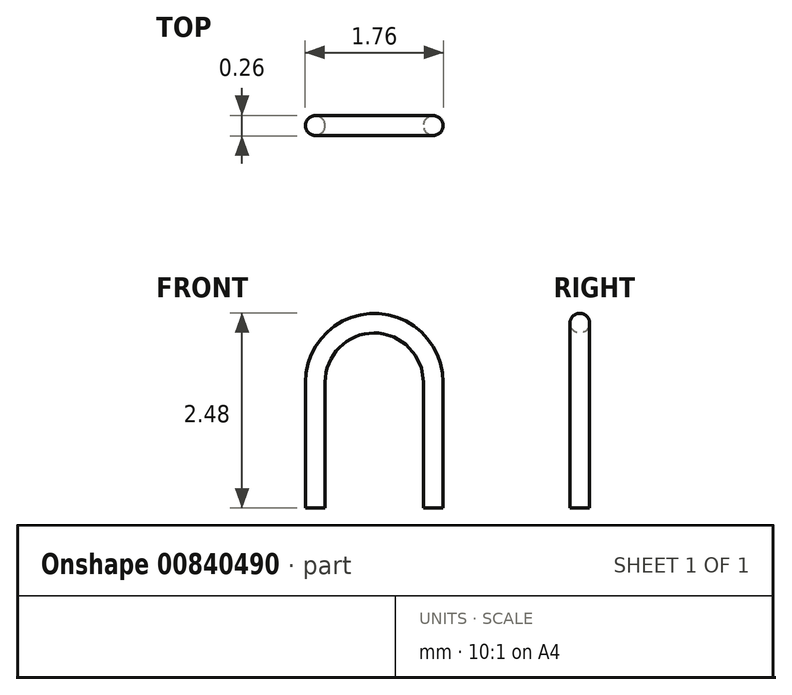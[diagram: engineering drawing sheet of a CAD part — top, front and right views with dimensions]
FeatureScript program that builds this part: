
annotation { "Feature Type Name" : "Feature", "Feature Type Description" : "" }
export const myFeature = defineFeature(function(context is Context, id is Id, definition is map)
    precondition{}
    {
        {
            var Q0;
            Q0=qCreatedBy(makeId("Front.planeOp"),FACE);
            var sketch = newSketch(context, id + "F0", { "sketchPlane" : qUnion([Q0])});
            skLineSegment(sketch, "E0", {"start": v(0.75, 0) * mm, "end": v(0.75, 1.6) * mm});
            skArc(sketch, "E1", {"start": v(0.75, 1.6) * mm, "mid": v(0, 2.35) * mm, "end": v(-0.75, 1.6) * mm});
            skLineSegment(sketch, "E2", {"start": v(-0.75, 1.6) * mm, "end": v(-0.75, 0) * mm});
            skSolve(sketch);
        }
        {
            var Q0;
            Q0=qCreatedBy(makeId("Top.planeOp"),FACE);
            var sketch = newSketch(context, id + "F1", { "sketchPlane" : qUnion([Q0])});
            skCircle(sketch, "E3", {"center": v(0.75, 0) * mm, "radius": 0.12 * mm});
            skSolve(sketch);
        }
        {
            var Q0;
            Q0=makeQuery(id+"F1.imprint","IMPRINT",FACE,{"disambiguationData":[TD([[makeQuery(id+"F1.imprint","IMPRINT",EDGE,{"derivedFrom":sQuery(id+"F1.wireOp",EDGE,"E3")}),1.0]])]});
            var Q1;
            Q1 = qConstructionFilter(qBodyType(qCreatedBy(id + "F0" ,EDGE), BodyType.WIRE), ConstructionObject.NO);
            sweep(context, id + "F2", {"profiles" : qUnion([Q0]), "path" : qUnion([Q1])});
        }
    });
